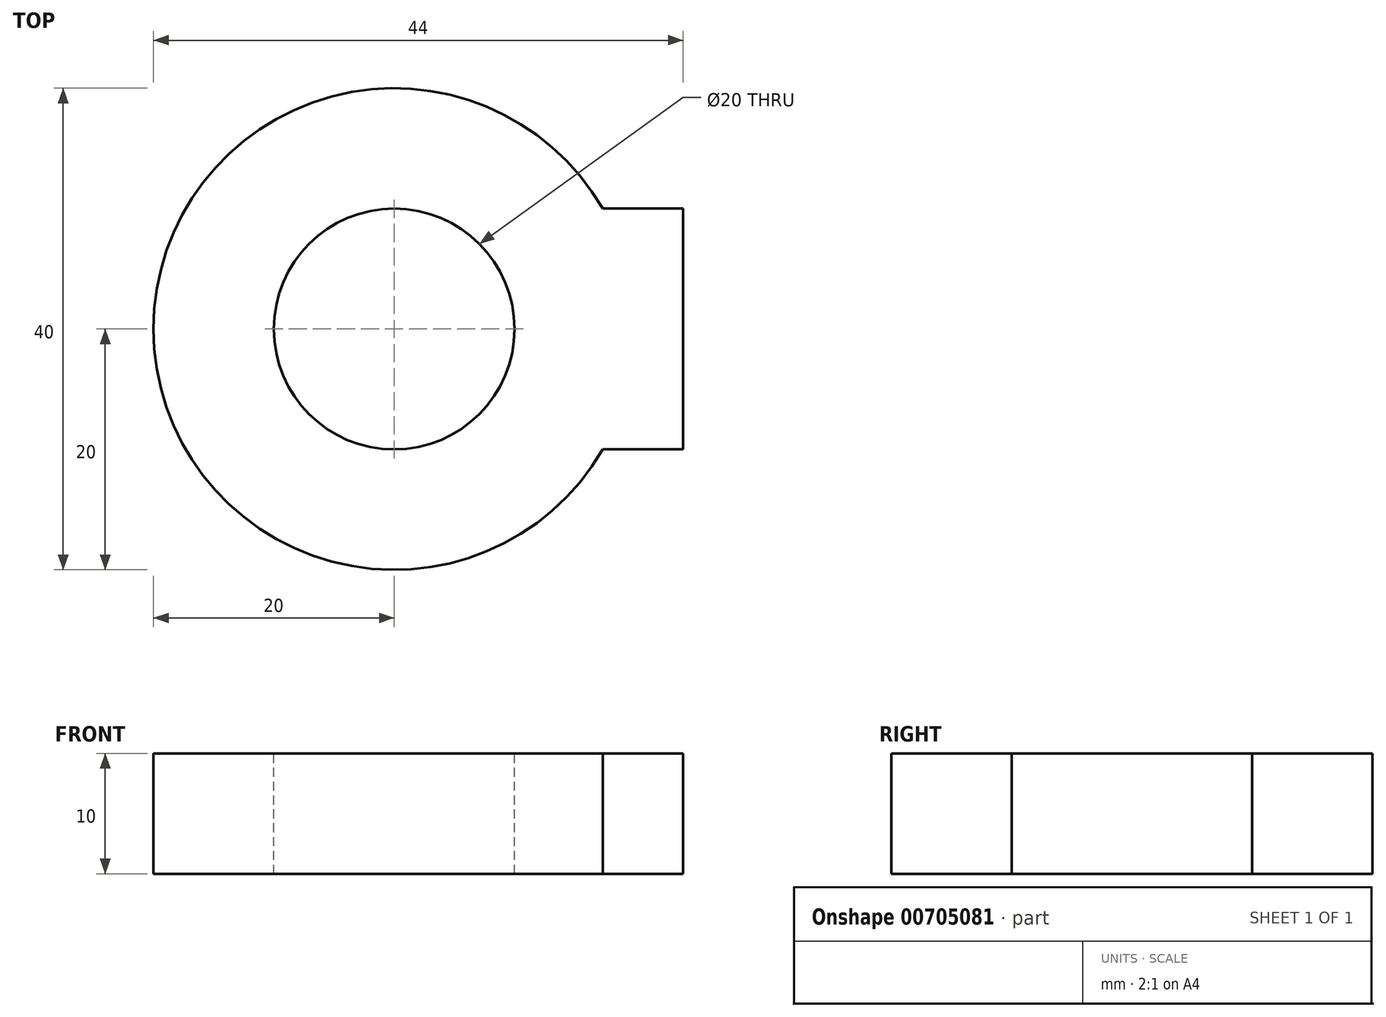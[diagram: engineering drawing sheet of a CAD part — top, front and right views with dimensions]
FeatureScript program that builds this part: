
annotation { "Feature Type Name" : "Feature", "Feature Type Description" : "" }
export const myFeature = defineFeature(function(context is Context, id is Id, definition is map)
    precondition{}
    {
        {
            var Q0;
            Q0=qCreatedBy(makeId("Top.planeOp"),FACE);
            var sketch = newSketch(context, id + "F0", { "sketchPlane" : qUnion([Q0])});
            skCircle(sketch, "E0", {"center": v(20, 20) * mm, "radius": 20 * mm});
            skLineSegment(sketch, "E1.bottom", {"start": v(44, 30) * mm, "end": v(20, 30) * mm});
            skLineSegment(sketch, "E1.top", {"start": v(44, 10) * mm, "end": v(20, 10) * mm});
            skLineSegment(sketch, "E1.left", {"start": v(44, 30) * mm, "end": v(44, 10) * mm});
            skLineSegment(sketch, "E1.right", {"start": v(20, 30) * mm, "end": v(20, 10) * mm});
            skSolve(sketch);
        }
        {
            var Q0;
            Q0 = qSketchRegion(id + "F0", true);
            extrude(context, id + "F1", {"entities" : qUnion([Q0]), "depth" : 10 * mm, "offsetDistance" : 25 * mm});
        }
        {
            var Q0;
            Q0=makeQuery(id+"F1.opExtrude","CAP_FACE",FACE,{"disambiguationData":[OSD([sQuery(id+"F0.wireOp",EDGE,"E0"),sQuery(id+"F0.wireOp",EDGE,"E1.bottom"),sQuery(id+"F0.wireOp",EDGE,"E1.top"),sQuery(id+"F0.wireOp",EDGE,"E1.left")])],"isStart":false});
            var sketch = newSketch(context, id + "F2", { "sketchPlane" : qUnion([Q0])});
            skCircle(sketch, "E2", {"center": v(20, 20) * mm, "radius": 10 * mm});
            skSolve(sketch);
        }
        {
            var Q0;
            Q0 = qSketchRegion(id + "F2", true);
            extrude(context, id + "F3", {"entities" : qUnion([Q0]), "operationType" : NewBodyOperationType.REMOVE, "oppositeDirection" : true, "depth" : 10 * mm, "offsetDistance" : 25 * mm});
        }
    });
